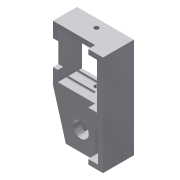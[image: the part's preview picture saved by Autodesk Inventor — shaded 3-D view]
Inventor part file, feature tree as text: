
AUTODESK INVENTOR PART (.ipt)
format: ipt  version: 2019.4 (Build 234330000, 330)  size: 218,112 bytes
history: native  units: mm
features: reference x14, sketch x5, extrude x5, other x3, plane x2, projected_geometry x2
ambient origin geometry x8: Origin, YZ Plane, XZ Plane, XY Plane, X Axis, Y Axis, Z Axis, Center Point
bodies: Solid1 (feature_tree)
feature tree (31):
  sketch  "Sketch1"  dims[d0=0.1mm d1=0.2mm]
  plane  "Work Plane1"
  extrude  "Extrusion1"  Depth=0.2mm
  sketch  "Sketch2"  dims[d2=3.0mm d3=3.0mm]
  plane  "Work Plane2"
  extrude  "Extrusion2"  Depth=3.0mm
  extrude  "Extrusion3"  Depth=3.0mm
  extrude  "Extrusion4"  Depth=3.0mm
  extrude  "Extrusion5"  Depth=18.2mm
  reference  "Reference1"
  reference  "Reference2"
  reference  "Reference3"
  reference  "Reference4"
  reference  "Reference5"
  reference  "Reference6"
  reference  "Reference7"
  reference  "Reference8"
  reference  "Reference9"
  projected_geometry  "Projected Loop1"
  reference  "Reference10"
  sketch  "Sketch3"  dims[d4=3.0mm d5=3.0mm]
  reference  "Reference11"
  reference  "Reference12"
  sketch  "Sketch4"  dims[d6=3.0mm d7=3.0mm]
  reference  "Reference13"
  sketch  "Sketch5"  dims[d8=10.0mm d9=0.0mm d10=18.2mm d11=10.0mm d12=0.0mm d13=2.8mm d14=2.8mm d15=20.0mm d16=0.0mm d17=20.0mm d18=0.0mm d19=20.0mm d20=0.0mm]
  projected_geometry  "Projected Loop2"
  reference  "Reference14"
  other  "Assembly_Nema_Motor_attachement_for_XYstage.iam"
  other  "00_NEMA11:1"
  other  "00_micrometer_moun_xystage_china:1"
